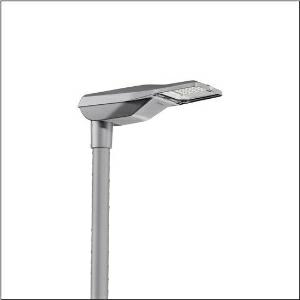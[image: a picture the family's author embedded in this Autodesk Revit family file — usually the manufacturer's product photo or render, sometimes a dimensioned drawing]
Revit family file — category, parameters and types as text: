
# Revit family: streetlight_sl_21_micro___st1_5a_5xe5p33a08db_61e9
name_source: partatom
category: Lighting Fixtures
units: mm (PartAtom-declared; Revit-internal decimal feet)

## family parameters
Cut with Voids When Loaded = No
Host = Face
Light Source = No
Part Type = Normal
Room Calculation Point = No
Round Connector Dimension = Use Diameter
Shared = No

## types (1)
- --- (1 x LED, 5020 lm, 39.1 W, 3000K)
    Apparent Load = 39 VA
    CIE Flux Codes = 22 53 95 100 100
    Color Rendering = 70
    Color Temperature = 3000K
    Default Elevation = 1800 mm
    Description = Streetlight SL 21 micro, mast luminaire, primary light control with lens, of PMMA, primary optical cover: cover, of toughened safety glass, transparent, light distribution: ST1.5a, light emission: direct distribution, primary light characteristic: asymmetric, installation type: side-entry, post-top, LED, 3G 1.5mm², High Power LED, rated luminous flux: 5.020lm, luminous efficacy: 128lm/W, light colour: 730, colour temperature: 3000K, control gear: Easy, control: flexible luminous flux parameterisation, time-dependent luminous flux control, constant luminous flux control, overheat protection, mains connection: 230..240V, AC, 50/60Hz, connection cable pre-assembled, cable length: 6,5m, wiring characteristics: H07RN-F, start of lifetime: 39W, end of service life: 41W, reduction: 18W, luminaire housing, of diecast aluminium, powder-coated, Siteco® metallic grey (DB 702S), corrosivity category C5 mid according to DIN EN ISO 12944, please order mast flange separately, inclination adjustable: 0°, 5°, 10°, 15°, sealing non-destructively replaceable, multi-level sealing system, length: 528mm, width: 235mm, height: 110mm, mast flange for spigot size: 42mm (side-entry): 5XC10008XM4, 60/48mm (side-entry/post-top): 5XC10108XM2, 76/60mm (side-entry/post-top): 5XC10108XM1, protection rating (complete): IP66, insulation class (complete): insulation class II (safety insulation), certification: CE, ENEC, ENEC+, VDE, impact resistance: IK10, permissible operating ambient temperature for outdoor applications: -40..+50°C, standard-compliant lighting for roads and squares, packaging unit: 1 piece

Light Distribution: ST1.5a
    Height = 110 mm
    Lamp = 1 x LED
    Lamp Light Flux = 5020 lm
    Lamp Power = 39.1 W
    Lamp count = 1
    Length = 528 mm
    Luminous efficacy = 128 lm/W
    Manufacturer = Siteco
    ModVariant = No
    Model = 5XE5P33A08DB
    Number of Poles = 1
    OnlyDefault = Yes
    Power Factor = 1
    Product Name = Streetlight SL 21 micro | ST1.5a
    Product group = mast luminaire | pylon top
    ProductGroupID = 6100
    Protection Class = Protection class II
    Protection Degree = IP 66
    RLX_Detail_Level = 1
    RLX_Emergency_Light_Flux = 0 lm
    RLX_Emergency_Type = 0
    RLX_Emergency_Type_DB = No
    RlxData = <blob elided: 102661 chars, md5=bb99f622>
    Socket = socket
    Standby Power = 0 W
    System Light Flux = 5020 lm
    System Power = 39 W
    Type Comments = factory setting: luminous flux: 100 % | Output Level: 100 % | 765 mA
    Type Image = l_1006881.jpg
    URL = http://relux.com
    VarID = @adj_153610
    Voltage = 0 V
    Weight = 0.00 kg
    Width = 235 mm

## geometry (parser evidence)
native form markers: Blend x4, Sweep x12
no freeform markers — native parametric forms only
